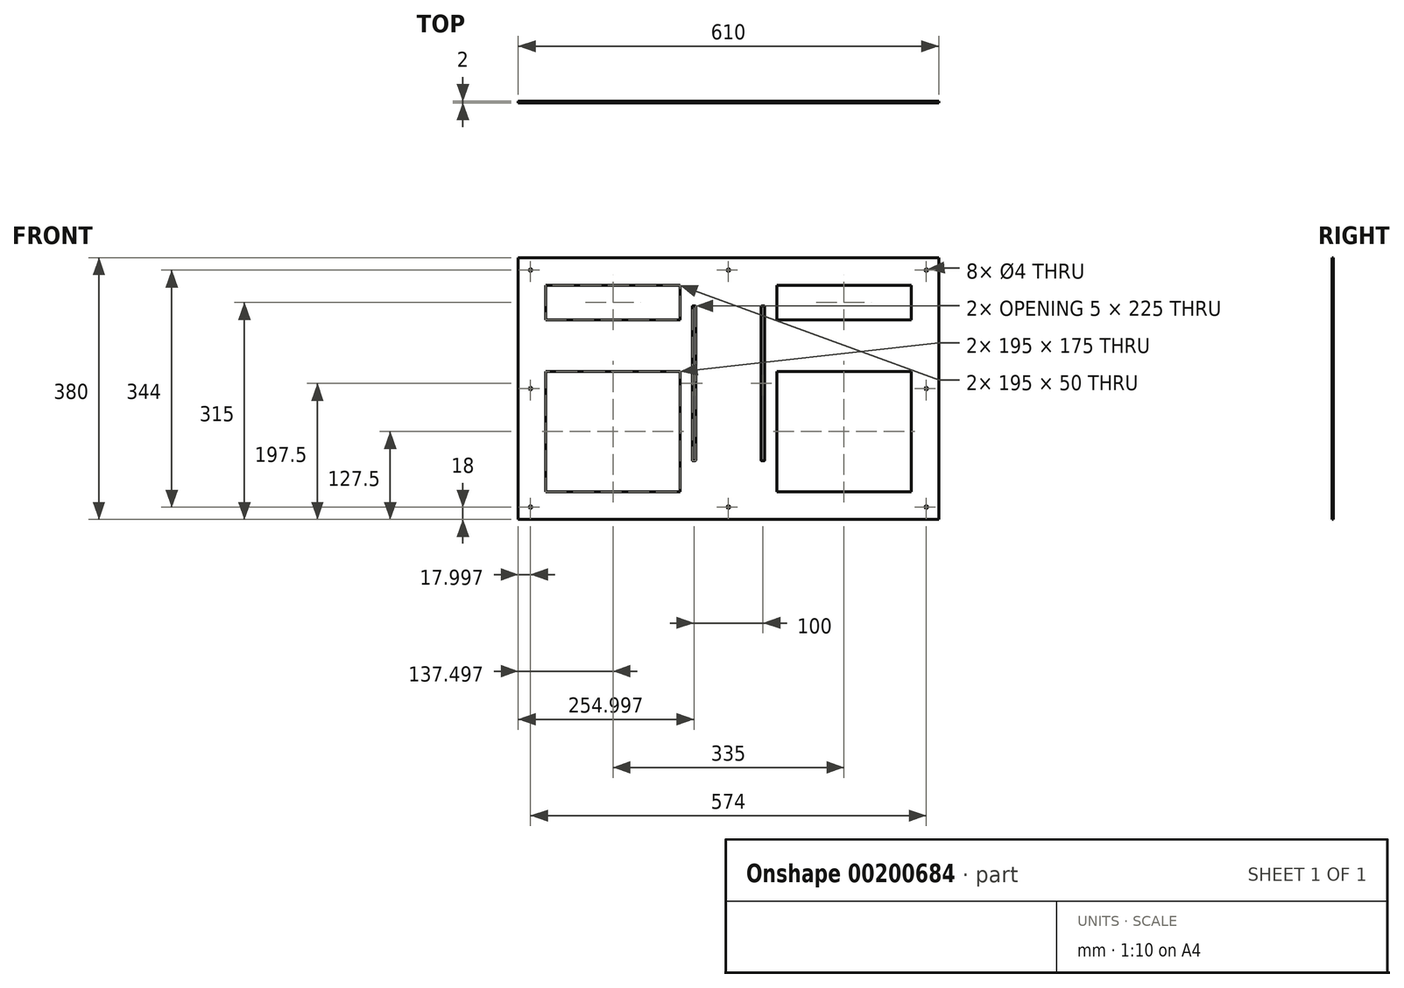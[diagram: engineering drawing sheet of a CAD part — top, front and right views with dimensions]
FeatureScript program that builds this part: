
annotation { "Feature Type Name" : "Feature", "Feature Type Description" : "" }
export const myFeature = defineFeature(function(context is Context, id is Id, definition is map)
    precondition{}
    {
        {
            var Q0;
            Q0=qCreatedBy(makeId("Front.planeOp"),FACE);
            var sketch = newSketch(context, id + "F0", { "sketchPlane" : qUnion([Q0])});
            skLineSegment(sketch, "E0.bottom", {"start": v(-244.64, 150) * mm, "end": v(-49.64, 150) * mm});
            skLineSegment(sketch, "E0.top", {"start": v(-244.64, -150) * mm, "end": v(-49.64, -150) * mm});
            skLineSegment(sketch, "E0.left", {"start": v(-244.64, 150) * mm, "end": v(-244.64, 100) * mm});
            skLineSegment(sketch, "E0.right", {"start": v(285.36, 150) * mm, "end": v(285.36, 100) * mm});
            skLineSegment(sketch, "E1", {"start": v(-284.64, 190) * mm, "end": v(325.36, 190) * mm});
            skLineSegment(sketch, "E2", {"start": v(325.36, 190) * mm, "end": v(325.36, -190) * mm});
            skLineSegment(sketch, "E3", {"start": v(325.36, -190) * mm, "end": v(-284.64, -190) * mm});
            skLineSegment(sketch, "E4", {"start": v(-284.64, 190) * mm, "end": v(-284.64, -190) * mm});
            skPoint(sketch, "E5", {"position": v(-266.64, 172) * mm});
            skPoint(sketch, "E6", {"position": v(307.36, 172) * mm});
            skPoint(sketch, "E7", {"position": v(-266.64, -172) * mm});
            skPoint(sketch, "E8", {"position": v(307.36, -172) * mm});
            skCircle(sketch, "E9", {"center": v(-266.64, 172) * mm, "radius": 2 * mm});
            skCircle(sketch, "E10", {"center": v(-266.64, -172) * mm, "radius": 2 * mm});
            skCircle(sketch, "E11", {"center": v(307.36, -172) * mm, "radius": 2 * mm});
            skCircle(sketch, "E12", {"center": v(307.36, 172) * mm, "radius": 2 * mm});
            skPoint(sketch, "E13", {"position": v(20.36, 172) * mm});
            skPoint(sketch, "E13.positionSnap0", {"position": v(20.36, 190) * mm});
            skPoint(sketch, "E14", {"position": v(20.36, -172) * mm});
            skPoint(sketch, "E14.positionSnap0", {"position": v(20.36, -190) * mm});
            skPoint(sketch, "E15", {"position": v(-266.64, 0) * mm});
            skPoint(sketch, "E15.positionSnap0", {"position": v(-284.64, 0) * mm});
            skPoint(sketch, "E16", {"position": v(307.36, 0) * mm});
            skPoint(sketch, "E16.positionSnap0", {"position": v(-244.64, 0) * mm});
            skCircle(sketch, "E17", {"center": v(-266.64, 0) * mm, "radius": 2 * mm});
            skCircle(sketch, "E18", {"center": v(20.36, 172) * mm, "radius": 2 * mm});
            skCircle(sketch, "E19", {"center": v(307.36, 0) * mm, "radius": 2 * mm});
            skCircle(sketch, "E20", {"center": v(20.36, -172) * mm, "radius": 2 * mm});
            skLineSegment(sketch, "E21", {"start": v(-49.64, 150) * mm, "end": v(-49.64, 100) * mm});
            skLineSegment(sketch, "E22", {"start": v(90.36, 150) * mm, "end": v(90.36, 100) * mm});
            skLineSegment(sketch, "E23", {"start": v(-244.64, 100) * mm, "end": v(-49.64, 100) * mm});
            skLineSegment(sketch, "E24.trimOffspring", {"start": v(90.36, 150) * mm, "end": v(285.36, 150) * mm});
            skLineSegment(sketch, "E25.trimOffspring", {"start": v(-49.64, -40) * mm, "end": v(-49.64, -150) * mm});
            skLineSegment(sketch, "E26.trimOffspring", {"start": v(90.36, -40) * mm, "end": v(90.36, -150) * mm});
            skLineSegment(sketch, "E27.trimOffspring", {"start": v(-244.64, -40) * mm, "end": v(-244.64, -150) * mm});
            skLineSegment(sketch, "E28.trimOffspring", {"start": v(285.36, -40) * mm, "end": v(285.36, -150) * mm});
            skLineSegment(sketch, "E29.trimOffspring", {"start": v(90.36, 100) * mm, "end": v(285.36, 100) * mm});
            skLineSegment(sketch, "E30.trimOffspring", {"start": v(90.36, -150) * mm, "end": v(285.36, -150) * mm});
            skLineSegment(sketch, "E31.bottom", {"start": v(-31.14, 120) * mm, "end": v(-28.14, 120) * mm});
            skLineSegment(sketch, "E31.top", {"start": v(-31.14, -105) * mm, "end": v(-28.14, -105) * mm});
            skLineSegment(sketch, "E31.left", {"start": v(-32.14, 119) * mm, "end": v(-32.14, -104) * mm});
            skLineSegment(sketch, "E31.right", {"start": v(-27.14, 119) * mm, "end": v(-27.14, -104) * mm});
            skLineSegment(sketch, "E32.bottom", {"start": v(68.86, 120) * mm, "end": v(71.86, 120) * mm});
            skLineSegment(sketch, "E32.top", {"start": v(68.86, -105) * mm, "end": v(71.86, -105) * mm});
            skLineSegment(sketch, "E32.left", {"start": v(67.86, 119) * mm, "end": v(67.86, -104) * mm});
            skLineSegment(sketch, "E32.right", {"start": v(72.86, 119) * mm, "end": v(72.86, -104) * mm});
            skPoint(sketch, "E33.visualSharp", {"position": v(-32.14, 120) * mm});
            skArc(sketch, "E33.filletArc", {"start": v(-31.14, 120) * mm, "mid": v(-31.85, 119.7) * mm, "end": v(-32.14, 119) * mm});
            skPoint(sketch, "E34.visualSharp", {"position": v(-27.14, 120) * mm});
            skArc(sketch, "E34.filletArc", {"start": v(-27.14, 119) * mm, "mid": v(-27.44, 119.7) * mm, "end": v(-28.14, 120) * mm});
            skPoint(sketch, "E35.visualSharp", {"position": v(-27.14, -105) * mm});
            skArc(sketch, "E35.filletArc", {"start": v(-28.14, -105) * mm, "mid": v(-27.44, -104.7) * mm, "end": v(-27.14, -104) * mm});
            skPoint(sketch, "E36.visualSharp", {"position": v(-32.14, -105) * mm});
            skArc(sketch, "E36.filletArc", {"start": v(-32.14, -104) * mm, "mid": v(-31.85, -104.7) * mm, "end": v(-31.14, -105) * mm});
            skPoint(sketch, "E37.visualSharp", {"position": v(67.86, -105) * mm});
            skArc(sketch, "E37.filletArc", {"start": v(67.86, -104) * mm, "mid": v(68.15, -104.7) * mm, "end": v(68.86, -105) * mm});
            skPoint(sketch, "E38.visualSharp", {"position": v(72.86, -105) * mm});
            skArc(sketch, "E38.filletArc", {"start": v(71.86, -105) * mm, "mid": v(72.56, -104.7) * mm, "end": v(72.86, -104) * mm});
            skPoint(sketch, "E39.visualSharp", {"position": v(67.86, 120) * mm});
            skArc(sketch, "E39.filletArc", {"start": v(68.86, 120) * mm, "mid": v(68.15, 119.7) * mm, "end": v(67.86, 119) * mm});
            skPoint(sketch, "E40.visualSharp", {"position": v(72.86, 120) * mm});
            skArc(sketch, "E40.filletArc", {"start": v(72.86, 119) * mm, "mid": v(72.56, 119.7) * mm, "end": v(71.86, 120) * mm});
            skLineSegment(sketch, "E41.top", {"start": v(-244.64, 25) * mm, "end": v(-49.64, 25) * mm});
            skLineSegment(sketch, "E41.left", {"start": v(-244.64, -40) * mm, "end": v(-244.64, 25) * mm});
            skLineSegment(sketch, "E41.right", {"start": v(-49.64, -40) * mm, "end": v(-49.64, 25) * mm});
            skLineSegment(sketch, "E42.top", {"start": v(90.36, 25) * mm, "end": v(285.36, 25) * mm});
            skLineSegment(sketch, "E42.left", {"start": v(90.36, -40) * mm, "end": v(90.36, 25) * mm});
            skLineSegment(sketch, "E42.right", {"start": v(285.36, -40) * mm, "end": v(285.36, 25) * mm});
            skSolve(sketch);
        }
        {
            var Q0;
            Q0 = qSketchRegion(id + "F0", true);
            extrude(context, id + "F1", {"entities" : qUnion([Q0]), "depth" : 2 * mm});
        }
    });
